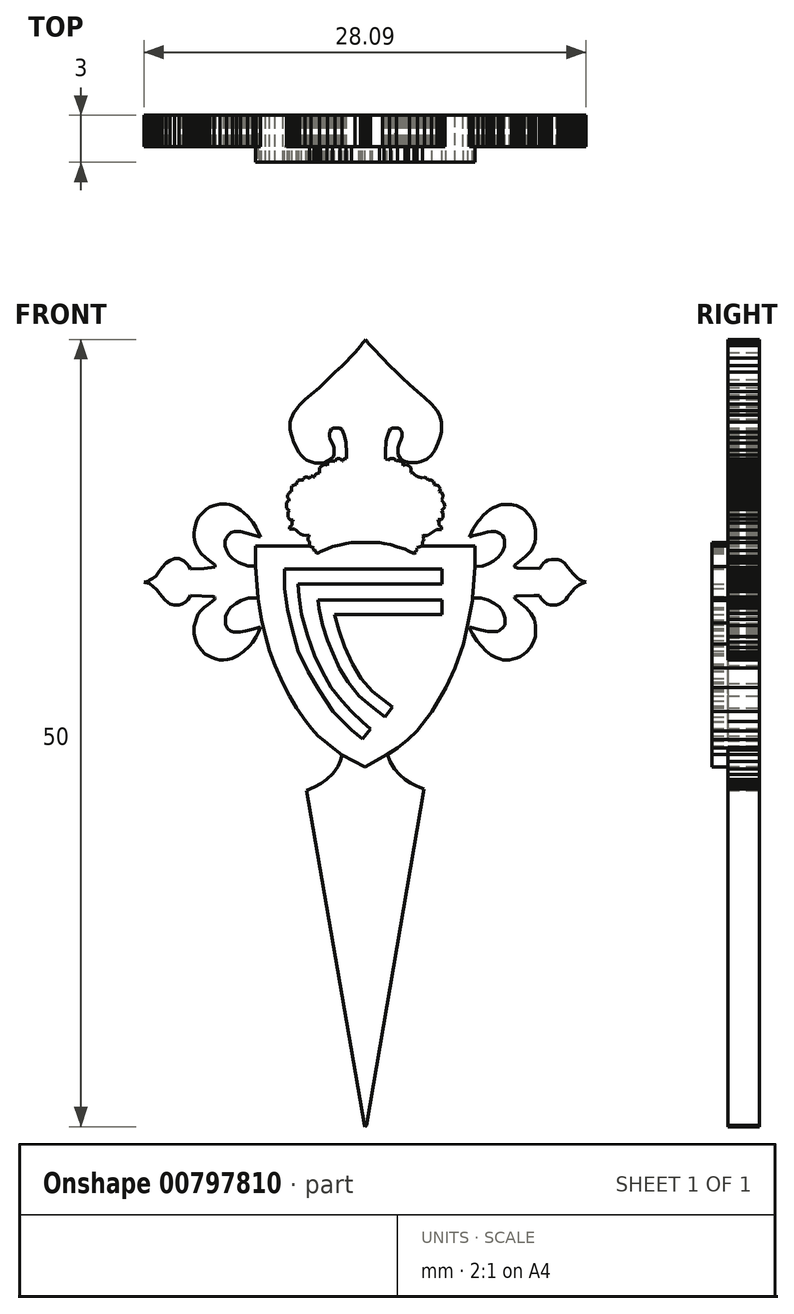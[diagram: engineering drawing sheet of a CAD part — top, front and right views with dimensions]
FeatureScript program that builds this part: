
annotation { "Feature Type Name" : "Feature", "Feature Type Description" : "" }
export const myFeature = defineFeature(function(context is Context, id is Id, definition is map)
    precondition{}
    {
        {
            var Q0;
            Q0=qCreatedBy(makeId("Front.planeOp"),FACE);
            var sketch = newSketch(context, id + "F0", { "sketchPlane" : qUnion([Q0])});
            skLineSegment(sketch, "E0", {"start": v(14.06, 0) * mm, "end": v(10.39, 21.27) * mm});
            skPoint(sketch, "E0.startSnap0", {"position": v(14.06, -0.08) * mm});
            skLineSegment(sketch, "E1", {"start": v(10.39, 21.27) * mm, "end": v(10.9, 21.5) * mm});
            skLineSegment(sketch, "E2", {"start": v(10.9, 21.5) * mm, "end": v(11.32, 21.71) * mm});
            skLineSegment(sketch, "E3", {"start": v(11.32, 21.71) * mm, "end": v(11.67, 21.99) * mm});
            skLineSegment(sketch, "E4", {"start": v(11.67, 21.99) * mm, "end": v(12.06, 22.35) * mm});
            skLineSegment(sketch, "E5", {"start": v(12.06, 22.35) * mm, "end": v(12.39, 22.8) * mm});
            skLineSegment(sketch, "E6", {"start": v(12.39, 22.8) * mm, "end": v(12.57, 23.17) * mm});
            skLineSegment(sketch, "E7", {"start": v(12.57, 23.17) * mm, "end": v(12.65, 23.55) * mm});
            skLineSegment(sketch, "E8", {"start": v(12.65, 23.55) * mm, "end": v(11.92, 24.1) * mm});
            skLineSegment(sketch, "E9", {"start": v(11.92, 24.1) * mm, "end": v(11.54, 24.4) * mm});
            skLineSegment(sketch, "E10", {"start": v(11.54, 24.4) * mm, "end": v(11.15, 24.74) * mm});
            skLineSegment(sketch, "E11", {"start": v(11.15, 24.74) * mm, "end": v(10.71, 25.21) * mm});
            skLineSegment(sketch, "E12", {"start": v(10.71, 25.21) * mm, "end": v(10.37, 25.64) * mm});
            skLineSegment(sketch, "E13", {"start": v(10.37, 25.64) * mm, "end": v(9.75, 26.5) * mm});
            skLineSegment(sketch, "E14", {"start": v(9.75, 26.5) * mm, "end": v(9.3, 27.27) * mm});
            skLineSegment(sketch, "E15", {"start": v(9.3, 27.27) * mm, "end": v(8.9, 28.06) * mm});
            skLineSegment(sketch, "E16", {"start": v(8.9, 28.06) * mm, "end": v(8.4, 29.21) * mm});
            skLineSegment(sketch, "E17", {"start": v(8.4, 29.21) * mm, "end": v(8.05, 30.15) * mm});
            skLineSegment(sketch, "E18", {"start": v(8.05, 30.15) * mm, "end": v(7.79, 31.09) * mm});
            skLineSegment(sketch, "E19", {"start": v(7.79, 31.09) * mm, "end": v(7.54, 32.09) * mm});
            skLineSegment(sketch, "E20", {"start": v(7.54, 32.09) * mm, "end": v(7.4, 32.9) * mm});
            skLineSegment(sketch, "E21", {"start": v(7.4, 32.9) * mm, "end": v(7.32, 33.46) * mm});
            skLineSegment(sketch, "E22", {"start": v(7.32, 33.46) * mm, "end": v(7.32, 33.5) * mm});
            skLineSegment(sketch, "E23", {"start": v(6.97, 33.5) * mm, "end": v(6.72, 33.5) * mm});
            skLineSegment(sketch, "E24", {"start": v(6.72, 33.5) * mm, "end": v(6.45, 33.4) * mm});
            skLineSegment(sketch, "E25", {"start": v(6.45, 33.4) * mm, "end": v(6.24, 33.33) * mm});
            skLineSegment(sketch, "E26", {"start": v(6.24, 33.33) * mm, "end": v(5.92, 33.16) * mm});
            skLineSegment(sketch, "E27", {"start": v(5.92, 33.16) * mm, "end": v(5.56, 32.88) * mm});
            skLineSegment(sketch, "E28", {"start": v(5.56, 32.88) * mm, "end": v(5.37, 32.61) * mm});
            skLineSegment(sketch, "E29", {"start": v(5.37, 32.61) * mm, "end": v(5.26, 32.32) * mm});
            skLineSegment(sketch, "E30", {"start": v(5.26, 32.32) * mm, "end": v(5.26, 31.8) * mm});
            skLineSegment(sketch, "E31", {"start": v(5.26, 31.8) * mm, "end": v(5.39, 31.56) * mm});
            skLineSegment(sketch, "E32", {"start": v(5.39, 31.56) * mm, "end": v(5.58, 31.4) * mm});
            skLineSegment(sketch, "E33", {"start": v(5.58, 31.4) * mm, "end": v(5.77, 31.33) * mm});
            skLineSegment(sketch, "E34", {"start": v(5.77, 31.33) * mm, "end": v(6.17, 31.33) * mm});
            skLineSegment(sketch, "E35", {"start": v(6.17, 31.33) * mm, "end": v(6.53, 31.4) * mm});
            skLineSegment(sketch, "E36", {"start": v(6.53, 31.4) * mm, "end": v(6.9, 31.49) * mm});
            skLineSegment(sketch, "E37", {"start": v(6.9, 31.49) * mm, "end": v(7.47, 31.64) * mm});
            skLineSegment(sketch, "E38", {"start": v(7.47, 31.64) * mm, "end": v(7.36, 31.33) * mm});
            skLineSegment(sketch, "E39", {"start": v(7.36, 31.33) * mm, "end": v(7.18, 31.03) * mm});
            skLineSegment(sketch, "E40", {"start": v(7.18, 31.03) * mm, "end": v(6.97, 30.68) * mm});
            skLineSegment(sketch, "E41", {"start": v(6.97, 30.68) * mm, "end": v(6.76, 30.46) * mm});
            skLineSegment(sketch, "E42", {"start": v(6.76, 30.46) * mm, "end": v(6.38, 30.1) * mm});
            skLineSegment(sketch, "E43", {"start": v(6.38, 30.1) * mm, "end": v(6.03, 29.84) * mm});
            skLineSegment(sketch, "E44", {"start": v(6.03, 29.84) * mm, "end": v(5.67, 29.65) * mm});
            skLineSegment(sketch, "E45", {"start": v(5.67, 29.65) * mm, "end": v(5.37, 29.6) * mm});
            skLineSegment(sketch, "E46", {"start": v(5.37, 29.6) * mm, "end": v(5.12, 29.56) * mm});
            skLineSegment(sketch, "E47", {"start": v(5.12, 29.56) * mm, "end": v(4.88, 29.56) * mm});
            skLineSegment(sketch, "E48", {"start": v(4.88, 29.56) * mm, "end": v(4.65, 29.63) * mm});
            skLineSegment(sketch, "E49", {"start": v(4.65, 29.63) * mm, "end": v(4.4, 29.72) * mm});
            skLineSegment(sketch, "E50", {"start": v(4.4, 29.72) * mm, "end": v(3.96, 29.96) * mm});
            skLineSegment(sketch, "E51", {"start": v(3.96, 29.96) * mm, "end": v(3.7, 30.22) * mm});
            skLineSegment(sketch, "E52", {"start": v(3.7, 30.22) * mm, "end": v(3.45, 30.57) * mm});
            skLineSegment(sketch, "E53", {"start": v(3.45, 30.57) * mm, "end": v(3.3, 30.96) * mm});
            skLineSegment(sketch, "E54", {"start": v(3.3, 30.96) * mm, "end": v(3.24, 31.25) * mm});
            skLineSegment(sketch, "E55", {"start": v(3.24, 31.25) * mm, "end": v(3.24, 31.7) * mm});
            skLineSegment(sketch, "E56", {"start": v(3.51, 32.48) * mm, "end": v(3.7, 32.7) * mm});
            skLineSegment(sketch, "E57", {"start": v(3.7, 32.7) * mm, "end": v(3.89, 32.89) * mm});
            skLineSegment(sketch, "E58", {"start": v(3.89, 32.89) * mm, "end": v(4.12, 33.07) * mm});
            skLineSegment(sketch, "E59", {"start": v(4.12, 33.07) * mm, "end": v(4.55, 33.4) * mm});
            skLineSegment(sketch, "E60", {"start": v(4.55, 33.4) * mm, "end": v(4.58, 33.5) * mm});
            skLineSegment(sketch, "E61", {"start": v(4.58, 33.5) * mm, "end": v(4.55, 33.57) * mm});
            skLineSegment(sketch, "E62", {"start": v(4.55, 33.57) * mm, "end": v(4.45, 33.6) * mm});
            skLineSegment(sketch, "E63", {"start": v(4.45, 33.6) * mm, "end": v(3.02, 33.66) * mm});
            skLineSegment(sketch, "E64", {"start": v(3.02, 33.66) * mm, "end": v(2.88, 33.4) * mm});
            skLineSegment(sketch, "E65", {"start": v(2.88, 33.4) * mm, "end": v(2.7, 33.25) * mm});
            skLineSegment(sketch, "E66", {"start": v(2.7, 33.25) * mm, "end": v(2.47, 33.13) * mm});
            skLineSegment(sketch, "E67", {"start": v(2.47, 33.13) * mm, "end": v(2.3, 33.07) * mm});
            skLineSegment(sketch, "E68", {"start": v(2.3, 33.07) * mm, "end": v(1.97, 33.07) * mm});
            skLineSegment(sketch, "E69", {"start": v(1.97, 33.07) * mm, "end": v(1.73, 33.12) * mm});
            skLineSegment(sketch, "E70", {"start": v(1.73, 33.12) * mm, "end": v(1.59, 33.23) * mm});
            skLineSegment(sketch, "E71", {"start": v(1.59, 33.23) * mm, "end": v(1.39, 33.4) * mm});
            skLineSegment(sketch, "E72", {"start": v(1.39, 33.4) * mm, "end": v(1.1, 33.76) * mm});
            skLineSegment(sketch, "E73", {"start": v(1.1, 33.76) * mm, "end": v(0.87, 34.05) * mm});
            skLineSegment(sketch, "E74", {"start": v(0.87, 34.05) * mm, "end": v(0.66, 34.23) * mm});
            skLineSegment(sketch, "E75", {"start": v(0.66, 34.23) * mm, "end": v(0.41, 34.4) * mm});
            skLineSegment(sketch, "E76", {"start": v(0.41, 34.4) * mm, "end": v(0.14, 34.49) * mm});
            skLineSegment(sketch, "E77", {"start": v(0.14, 34.49) * mm, "end": v(0.06, 34.5) * mm});
            skLineSegment(sketch, "E78", {"start": v(0.06, 34.5) * mm, "end": v(0.14, 34.52) * mm});
            skLineSegment(sketch, "E79", {"start": v(0.14, 34.52) * mm, "end": v(0.25, 34.55) * mm});
            skLineSegment(sketch, "E80", {"start": v(0.25, 34.55) * mm, "end": v(0.35, 34.59) * mm});
            skLineSegment(sketch, "E81", {"start": v(0.35, 34.59) * mm, "end": v(0.43, 34.64) * mm});
            skLineSegment(sketch, "E82", {"start": v(0.43, 34.64) * mm, "end": v(0.62, 34.74) * mm});
            skLineSegment(sketch, "E83", {"start": v(0.62, 34.74) * mm, "end": v(0.82, 34.91) * mm});
            skLineSegment(sketch, "E84", {"start": v(0.82, 34.91) * mm, "end": v(1.02, 35.17) * mm});
            skLineSegment(sketch, "E85", {"start": v(1.02, 35.17) * mm, "end": v(1.22, 35.44) * mm});
            skLineSegment(sketch, "E86", {"start": v(1.22, 35.44) * mm, "end": v(1.46, 35.7) * mm});
            skLineSegment(sketch, "E87", {"start": v(1.46, 35.7) * mm, "end": v(1.72, 35.9) * mm});
            skLineSegment(sketch, "E88", {"start": v(1.72, 35.9) * mm, "end": v(2, 36) * mm});
            skLineSegment(sketch, "E89", {"start": v(2, 36) * mm, "end": v(2.3, 36) * mm});
            skLineSegment(sketch, "E90", {"start": v(2.3, 36) * mm, "end": v(2.6, 35.84) * mm});
            skLineSegment(sketch, "E91", {"start": v(2.6, 35.84) * mm, "end": v(2.8, 35.67) * mm});
            skLineSegment(sketch, "E92", {"start": v(2.8, 35.67) * mm, "end": v(2.93, 35.5) * mm});
            skLineSegment(sketch, "E93", {"start": v(2.93, 35.5) * mm, "end": v(3.02, 35.35) * mm});
            skLineSegment(sketch, "E94", {"start": v(3.02, 35.35) * mm, "end": v(3.89, 35.39) * mm});
            skLineSegment(sketch, "E95", {"start": v(3.89, 35.39) * mm, "end": v(4.58, 35.46) * mm});
            skLineSegment(sketch, "E96", {"start": v(4.58, 35.46) * mm, "end": v(4.58, 35.56) * mm});
            skLineSegment(sketch, "E97", {"start": v(4.58, 35.56) * mm, "end": v(4.55, 35.62) * mm});
            skLineSegment(sketch, "E98", {"start": v(4.55, 35.62) * mm, "end": v(4.3, 35.8) * mm});
            skLineSegment(sketch, "E99", {"start": v(4.3, 35.8) * mm, "end": v(3.97, 36.09) * mm});
            skLineSegment(sketch, "E100", {"start": v(3.97, 36.09) * mm, "end": v(3.7, 36.33) * mm});
            skLineSegment(sketch, "E101", {"start": v(3.7, 36.33) * mm, "end": v(3.5, 36.6) * mm});
            skLineSegment(sketch, "E102", {"start": v(3.5, 36.6) * mm, "end": v(3.35, 36.91) * mm});
            skLineSegment(sketch, "E103", {"start": v(3.35, 36.91) * mm, "end": v(3.28, 37.17) * mm});
            skLineSegment(sketch, "E104", {"start": v(3.28, 37.17) * mm, "end": v(3.23, 37.4) * mm});
            skLineSegment(sketch, "E105", {"start": v(3.23, 37.4) * mm, "end": v(3.23, 37.58) * mm});
            skLineSegment(sketch, "E106", {"start": v(3.23, 37.58) * mm, "end": v(3.28, 37.88) * mm});
            skLineSegment(sketch, "E107", {"start": v(3.28, 37.88) * mm, "end": v(3.34, 38.12) * mm});
            skLineSegment(sketch, "E108", {"start": v(3.34, 38.12) * mm, "end": v(3.42, 38.4) * mm});
            skLineSegment(sketch, "E109", {"start": v(3.42, 38.4) * mm, "end": v(3.57, 38.67) * mm});
            skLineSegment(sketch, "E110", {"start": v(3.57, 38.67) * mm, "end": v(3.78, 38.9) * mm});
            skLineSegment(sketch, "E111", {"start": v(3.78, 38.9) * mm, "end": v(4.02, 39.12) * mm});
            skLineSegment(sketch, "E112", {"start": v(4.02, 39.12) * mm, "end": v(4.25, 39.27) * mm});
            skLineSegment(sketch, "E113", {"start": v(4.25, 39.27) * mm, "end": v(4.52, 39.38) * mm});
            skLineSegment(sketch, "E114", {"start": v(4.91, 39.48) * mm, "end": v(5.32, 39.48) * mm});
            skLineSegment(sketch, "E115", {"start": v(5.32, 39.48) * mm, "end": v(5.5, 39.43) * mm});
            skLineSegment(sketch, "E116", {"start": v(5.5, 39.43) * mm, "end": v(5.7, 39.36) * mm});
            skLineSegment(sketch, "E117", {"start": v(5.7, 39.36) * mm, "end": v(5.94, 39.25) * mm});
            skLineSegment(sketch, "E118", {"start": v(5.94, 39.25) * mm, "end": v(6.2, 39.1) * mm});
            skLineSegment(sketch, "E119", {"start": v(6.66, 38.7) * mm, "end": v(7, 38.3) * mm});
            skLineSegment(sketch, "E120", {"start": v(7, 38.3) * mm, "end": v(7.19, 37.98) * mm});
            skLineSegment(sketch, "E121", {"start": v(7.19, 37.98) * mm, "end": v(7.48, 37.38) * mm});
            skLineSegment(sketch, "E122", {"start": v(7.48, 37.38) * mm, "end": v(6.43, 37.67) * mm});
            skLineSegment(sketch, "E123", {"start": v(6.43, 37.67) * mm, "end": v(6.22, 37.73) * mm});
            skLineSegment(sketch, "E124", {"start": v(6.22, 37.73) * mm, "end": v(5.83, 37.73) * mm});
            skLineSegment(sketch, "E125", {"start": v(5.83, 37.73) * mm, "end": v(5.6, 37.67) * mm});
            skLineSegment(sketch, "E126", {"start": v(5.6, 37.67) * mm, "end": v(5.4, 37.48) * mm});
            skLineSegment(sketch, "E127", {"start": v(5.4, 37.48) * mm, "end": v(5.27, 37.27) * mm});
            skLineSegment(sketch, "E128", {"start": v(5.27, 37.27) * mm, "end": v(5.23, 37.12) * mm});
            skLineSegment(sketch, "E129", {"start": v(5.23, 37.12) * mm, "end": v(5.23, 36.8) * mm});
            skLineSegment(sketch, "E130", {"start": v(5.23, 36.8) * mm, "end": v(5.31, 36.55) * mm});
            skLineSegment(sketch, "E131", {"start": v(5.31, 36.55) * mm, "end": v(5.48, 36.23) * mm});
            skLineSegment(sketch, "E132", {"start": v(5.48, 36.23) * mm, "end": v(5.7, 36) * mm});
            skLineSegment(sketch, "E133", {"start": v(5.7, 36) * mm, "end": v(6.08, 35.75) * mm});
            skLineSegment(sketch, "E134", {"start": v(6.08, 35.75) * mm, "end": v(6.67, 35.52) * mm});
            skLineSegment(sketch, "E135", {"start": v(6.67, 35.52) * mm, "end": v(7.16, 35.52) * mm});
            skLineSegment(sketch, "E136", {"start": v(7.16, 35.52) * mm, "end": v(7.16, 36.8) * mm});
            skLineSegment(sketch, "E137", {"start": v(10.58, 36.8) * mm, "end": v(10.58, 37.07) * mm});
            skLineSegment(sketch, "E138", {"start": v(10.58, 37.07) * mm, "end": v(10.48, 37.16) * mm});
            skLineSegment(sketch, "E139", {"start": v(10.48, 37.16) * mm, "end": v(10.48, 37.34) * mm});
            skLineSegment(sketch, "E140", {"start": v(10.48, 37.34) * mm, "end": v(10.54, 37.4) * mm});
            skLineSegment(sketch, "E141", {"start": v(10.54, 37.4) * mm, "end": v(10.54, 37.5) * mm});
            skLineSegment(sketch, "E142", {"start": v(10.54, 37.5) * mm, "end": v(10.35, 37.47) * mm});
            skLineSegment(sketch, "E143", {"start": v(10.35, 37.47) * mm, "end": v(10.17, 37.49) * mm});
            skLineSegment(sketch, "E144", {"start": v(10.17, 37.49) * mm, "end": v(10.01, 37.57) * mm});
            skLineSegment(sketch, "E145", {"start": v(10.01, 37.57) * mm, "end": v(9.86, 37.7) * mm});
            skLineSegment(sketch, "E146", {"start": v(9.86, 37.7) * mm, "end": v(9.72, 37.8) * mm});
            skLineSegment(sketch, "E147", {"start": v(9.72, 37.8) * mm, "end": v(9.64, 37.87) * mm});
            skLineSegment(sketch, "E148", {"start": v(9.64, 37.87) * mm, "end": v(9.3, 37.87) * mm});
            skLineSegment(sketch, "E149", {"start": v(9.3, 37.87) * mm, "end": v(9.3, 38) * mm});
            skLineSegment(sketch, "E150", {"start": v(9.3, 38) * mm, "end": v(9.48, 38.14) * mm});
            skLineSegment(sketch, "E151", {"start": v(9.48, 38.14) * mm, "end": v(9.48, 38.37) * mm});
            skLineSegment(sketch, "E152", {"start": v(9.48, 38.37) * mm, "end": v(9.54, 38.4) * mm});
            skLineSegment(sketch, "E153", {"start": v(9.54, 38.4) * mm, "end": v(9.54, 38.45) * mm});
            skLineSegment(sketch, "E154", {"start": v(9.54, 38.45) * mm, "end": v(9.43, 38.45) * mm});
            skLineSegment(sketch, "E155", {"start": v(9.43, 38.45) * mm, "end": v(9.34, 38.5) * mm});
            skLineSegment(sketch, "E156", {"start": v(9.34, 38.5) * mm, "end": v(9.3, 38.53) * mm});
            skLineSegment(sketch, "E157", {"start": v(9.3, 38.53) * mm, "end": v(9.2, 38.65) * mm});
            skLineSegment(sketch, "E158", {"start": v(9.2, 38.65) * mm, "end": v(9.2, 38.92) * mm});
            skLineSegment(sketch, "E159", {"start": v(9.2, 38.92) * mm, "end": v(9.24, 38.98) * mm});
            skLineSegment(sketch, "E160", {"start": v(9.24, 38.98) * mm, "end": v(9.3, 39.05) * mm});
            skLineSegment(sketch, "E161", {"start": v(9.3, 39.05) * mm, "end": v(9.22, 39.11) * mm});
            skLineSegment(sketch, "E162", {"start": v(9.22, 39.11) * mm, "end": v(9.13, 39.2) * mm});
            skLineSegment(sketch, "E163", {"start": v(9.13, 39.2) * mm, "end": v(9.1, 39.26) * mm});
            skLineSegment(sketch, "E164", {"start": v(9.1, 39.26) * mm, "end": v(9.1, 39.52) * mm});
            skLineSegment(sketch, "E165", {"start": v(9.1, 39.52) * mm, "end": v(9.13, 39.58) * mm});
            skLineSegment(sketch, "E166", {"start": v(9.13, 39.58) * mm, "end": v(9.18, 39.62) * mm});
            skLineSegment(sketch, "E167", {"start": v(9.18, 39.62) * mm, "end": v(9.23, 39.66) * mm});
            skLineSegment(sketch, "E168", {"start": v(9.23, 39.66) * mm, "end": v(9.3, 39.66) * mm});
            skLineSegment(sketch, "E169", {"start": v(9.3, 39.66) * mm, "end": v(9.3, 39.74) * mm});
            skLineSegment(sketch, "E170", {"start": v(9.3, 39.74) * mm, "end": v(9.25, 39.8) * mm});
            skLineSegment(sketch, "E171", {"start": v(9.25, 39.8) * mm, "end": v(9.2, 39.87) * mm});
            skLineSegment(sketch, "E172", {"start": v(9.2, 39.87) * mm, "end": v(9.2, 40.03) * mm});
            skLineSegment(sketch, "E173", {"start": v(9.2, 40.03) * mm, "end": v(9.24, 40.1) * mm});
            skLineSegment(sketch, "E174", {"start": v(9.24, 40.1) * mm, "end": v(9.27, 40.16) * mm});
            skLineSegment(sketch, "E175", {"start": v(9.27, 40.16) * mm, "end": v(9.33, 40.2) * mm});
            skLineSegment(sketch, "E176", {"start": v(9.33, 40.2) * mm, "end": v(9.38, 40.25) * mm});
            skLineSegment(sketch, "E177", {"start": v(9.38, 40.25) * mm, "end": v(9.43, 40.26) * mm});
            skLineSegment(sketch, "E178", {"start": v(9.43, 40.26) * mm, "end": v(9.43, 40.5) * mm});
            skLineSegment(sketch, "E179", {"start": v(9.43, 40.5) * mm, "end": v(9.48, 40.6) * mm});
            skLineSegment(sketch, "E180", {"start": v(9.48, 40.6) * mm, "end": v(9.59, 40.66) * mm});
            skLineSegment(sketch, "E181", {"start": v(9.59, 40.66) * mm, "end": v(9.64, 40.7) * mm});
            skLineSegment(sketch, "E182", {"start": v(9.64, 40.7) * mm, "end": v(9.77, 40.7) * mm});
            skLineSegment(sketch, "E183", {"start": v(9.77, 40.7) * mm, "end": v(9.77, 40.85) * mm});
            skLineSegment(sketch, "E184", {"start": v(9.77, 40.85) * mm, "end": v(9.8, 40.9) * mm});
            skLineSegment(sketch, "E185", {"start": v(9.8, 40.9) * mm, "end": v(9.86, 40.95) * mm});
            skLineSegment(sketch, "E186", {"start": v(9.86, 40.95) * mm, "end": v(9.9, 41) * mm});
            skLineSegment(sketch, "E187", {"start": v(9.9, 41) * mm, "end": v(10.14, 41) * mm});
            skLineSegment(sketch, "E188", {"start": v(10.14, 41) * mm, "end": v(10.21, 41.03) * mm});
            skLineSegment(sketch, "E189", {"start": v(10.21, 41.03) * mm, "end": v(10.21, 41.1) * mm});
            skLineSegment(sketch, "E190", {"start": v(10.21, 41.1) * mm, "end": v(10.27, 41.14) * mm});
            skLineSegment(sketch, "E191", {"start": v(10.27, 41.14) * mm, "end": v(10.34, 41.17) * mm});
            skLineSegment(sketch, "E192", {"start": v(10.34, 41.17) * mm, "end": v(10.42, 41.17) * mm});
            skLineSegment(sketch, "E193", {"start": v(10.42, 41.17) * mm, "end": v(10.47, 41.16) * mm});
            skLineSegment(sketch, "E194", {"start": v(10.47, 41.16) * mm, "end": v(10.54, 41.12) * mm});
            skLineSegment(sketch, "E195", {"start": v(10.54, 41.12) * mm, "end": v(10.58, 41.1) * mm});
            skLineSegment(sketch, "E196", {"start": v(10.58, 41.1) * mm, "end": v(10.6, 41.16) * mm});
            skLineSegment(sketch, "E197", {"start": v(10.6, 41.16) * mm, "end": v(10.65, 41.2) * mm});
            skLineSegment(sketch, "E198", {"start": v(10.65, 41.2) * mm, "end": v(10.7, 41.24) * mm});
            skLineSegment(sketch, "E199", {"start": v(10.7, 41.24) * mm, "end": v(10.74, 41.24) * mm});
            skLineSegment(sketch, "E200", {"start": v(10.74, 41.24) * mm, "end": v(10.8, 41.22) * mm});
            skLineSegment(sketch, "E201", {"start": v(10.8, 41.22) * mm, "end": v(10.84, 41.18) * mm});
            skLineSegment(sketch, "E202", {"start": v(10.84, 41.18) * mm, "end": v(10.89, 41.17) * mm});
            skLineSegment(sketch, "E203", {"start": v(10.89, 41.17) * mm, "end": v(10.89, 41.23) * mm});
            skLineSegment(sketch, "E204", {"start": v(10.89, 41.23) * mm, "end": v(10.92, 41.29) * mm});
            skLineSegment(sketch, "E205", {"start": v(10.92, 41.29) * mm, "end": v(10.94, 41.33) * mm});
            skLineSegment(sketch, "E206", {"start": v(10.94, 41.33) * mm, "end": v(11, 41.38) * mm});
            skLineSegment(sketch, "E207", {"start": v(11, 41.38) * mm, "end": v(11.05, 41.42) * mm});
            skLineSegment(sketch, "E208", {"start": v(11.05, 41.42) * mm, "end": v(11.1, 41.44) * mm});
            skLineSegment(sketch, "E209", {"start": v(11.1, 41.44) * mm, "end": v(11.23, 41.44) * mm});
            skLineSegment(sketch, "E210", {"start": v(11.23, 41.77) * mm, "end": v(11.28, 41.82) * mm});
            skLineSegment(sketch, "E211", {"start": v(11.28, 41.82) * mm, "end": v(11.33, 41.87) * mm});
            skLineSegment(sketch, "E212", {"start": v(11.33, 41.87) * mm, "end": v(11.4, 41.92) * mm});
            skLineSegment(sketch, "E213", {"start": v(11.4, 41.92) * mm, "end": v(11.47, 41.97) * mm});
            skLineSegment(sketch, "E214", {"start": v(11.47, 41.97) * mm, "end": v(11.66, 41.97) * mm});
            skLineSegment(sketch, "E215", {"start": v(11.66, 41.97) * mm, "end": v(11.73, 41.91) * mm});
            skLineSegment(sketch, "E216", {"start": v(11.73, 41.91) * mm, "end": v(11.73, 42.08) * mm});
            skLineSegment(sketch, "E217", {"start": v(11.73, 42.08) * mm, "end": v(11.86, 42.2) * mm});
            skLineSegment(sketch, "E218", {"start": v(11.86, 42.2) * mm, "end": v(12, 42.2) * mm});
            skLineSegment(sketch, "E219", {"start": v(12, 42.2) * mm, "end": v(12.13, 42.21) * mm});
            skLineSegment(sketch, "E220", {"start": v(12.13, 42.21) * mm, "end": v(12.2, 42.15) * mm});
            skLineSegment(sketch, "E221", {"start": v(12.2, 42.15) * mm, "end": v(12.23, 42.24) * mm});
            skLineSegment(sketch, "E222", {"start": v(12.23, 42.24) * mm, "end": v(12.28, 42.31) * mm});
            skLineSegment(sketch, "E223", {"start": v(12.28, 42.31) * mm, "end": v(12.34, 42.36) * mm});
            skLineSegment(sketch, "E224", {"start": v(12.34, 42.36) * mm, "end": v(12.5, 42.36) * mm});
            skLineSegment(sketch, "E225", {"start": v(12.5, 42.36) * mm, "end": v(12.6, 42.3) * mm});
            skLineSegment(sketch, "E226", {"start": v(12.6, 42.3) * mm, "end": v(12.66, 42.27) * mm});
            skLineSegment(sketch, "E227", {"start": v(12.66, 42.27) * mm, "end": v(12.67, 42.2) * mm});
            skLineSegment(sketch, "E228", {"start": v(12.67, 42.2) * mm, "end": v(12.7, 42.2) * mm});
            skLineSegment(sketch, "E229", {"start": v(12.7, 42.2) * mm, "end": v(12.7, 42.26) * mm});
            skLineSegment(sketch, "E230", {"start": v(12.7, 42.26) * mm, "end": v(12.77, 42.32) * mm});
            skLineSegment(sketch, "E231", {"start": v(12.77, 42.32) * mm, "end": v(12.85, 42.36) * mm});
            skLineSegment(sketch, "E232", {"start": v(12.85, 42.36) * mm, "end": v(12.94, 42.36) * mm});
            skLineSegment(sketch, "E233", {"start": v(12.94, 42.36) * mm, "end": v(12.94, 42.68) * mm});
            skLineSegment(sketch, "E234", {"start": v(12.94, 42.68) * mm, "end": v(12.88, 43.4) * mm});
            skLineSegment(sketch, "E235", {"start": v(12.88, 43.4) * mm, "end": v(12.76, 43.89) * mm});
            skLineSegment(sketch, "E236", {"start": v(12.76, 43.89) * mm, "end": v(12.64, 44.2) * mm});
            skLineSegment(sketch, "E237", {"start": v(12.64, 44.2) * mm, "end": v(12.48, 44.3) * mm});
            skLineSegment(sketch, "E238", {"start": v(12.48, 44.3) * mm, "end": v(12.11, 44.3) * mm});
            skLineSegment(sketch, "E239", {"start": v(12.11, 44.3) * mm, "end": v(11.98, 44.23) * mm});
            skLineSegment(sketch, "E240", {"start": v(11.98, 44.23) * mm, "end": v(11.89, 44.08) * mm});
            skLineSegment(sketch, "E241", {"start": v(11.89, 44.08) * mm, "end": v(11.85, 43.94) * mm});
            skLineSegment(sketch, "E242", {"start": v(11.85, 43.94) * mm, "end": v(11.85, 43.79) * mm});
            skLineSegment(sketch, "E243", {"start": v(11.85, 43.79) * mm, "end": v(11.9, 43.59) * mm});
            skLineSegment(sketch, "E244", {"start": v(12.1, 43.2) * mm, "end": v(12.14, 43.02) * mm});
            skLineSegment(sketch, "E245", {"start": v(12.14, 43.02) * mm, "end": v(12.14, 42.66) * mm});
            skLineSegment(sketch, "E246", {"start": v(12.14, 42.66) * mm, "end": v(12.1, 42.48) * mm});
            skLineSegment(sketch, "E247", {"start": v(12.1, 42.48) * mm, "end": v(11.93, 42.31) * mm});
            skLineSegment(sketch, "E248", {"start": v(11.93, 42.31) * mm, "end": v(11.73, 42.21) * mm});
            skLineSegment(sketch, "E249", {"start": v(11.73, 42.21) * mm, "end": v(11.61, 42.15) * mm});
            skLineSegment(sketch, "E250", {"start": v(11.61, 42.15) * mm, "end": v(11.46, 42.08) * mm});
            skLineSegment(sketch, "E251", {"start": v(11.46, 42.08) * mm, "end": v(10.94, 42.08) * mm});
            skLineSegment(sketch, "E252", {"start": v(10.94, 42.08) * mm, "end": v(10.74, 42.14) * mm});
            skLineSegment(sketch, "E253", {"start": v(10.74, 42.14) * mm, "end": v(10.54, 42.2) * mm});
            skLineSegment(sketch, "E254", {"start": v(10.54, 42.2) * mm, "end": v(10.4, 42.27) * mm});
            skLineSegment(sketch, "E255", {"start": v(10.4, 42.27) * mm, "end": v(10.22, 42.4) * mm});
            skLineSegment(sketch, "E256", {"start": v(10.22, 42.4) * mm, "end": v(10.09, 42.55) * mm});
            skLineSegment(sketch, "E257", {"start": v(10.09, 42.55) * mm, "end": v(9.91, 42.73) * mm});
            skLineSegment(sketch, "E258", {"start": v(9.57, 43.41) * mm, "end": v(9.5, 43.65) * mm});
            skLineSegment(sketch, "E259", {"start": v(9.5, 43.65) * mm, "end": v(9.43, 43.84) * mm});
            skLineSegment(sketch, "E260", {"start": v(9.43, 43.84) * mm, "end": v(9.34, 44.2) * mm});
            skLineSegment(sketch, "E261", {"start": v(9.34, 44.2) * mm, "end": v(9.34, 44.68) * mm});
            skLineSegment(sketch, "E262", {"start": v(9.34, 44.68) * mm, "end": v(9.38, 44.77) * mm});
            skLineSegment(sketch, "E263", {"start": v(9.38, 44.77) * mm, "end": v(9.4, 44.86) * mm});
            skLineSegment(sketch, "E264", {"start": v(9.4, 44.86) * mm, "end": v(9.5, 45.1) * mm});
            skLineSegment(sketch, "E265", {"start": v(9.5, 45.1) * mm, "end": v(9.6, 45.3) * mm});
            skLineSegment(sketch, "E266", {"start": v(9.6, 45.3) * mm, "end": v(9.7, 45.4) * mm});
            skLineSegment(sketch, "E267", {"start": v(9.7, 45.4) * mm, "end": v(9.85, 45.62) * mm});
            skLineSegment(sketch, "E268", {"start": v(9.85, 45.62) * mm, "end": v(9.96, 45.76) * mm});
            skLineSegment(sketch, "E269", {"start": v(9.96, 45.76) * mm, "end": v(10.3, 46.1) * mm});
            skLineSegment(sketch, "E270", {"start": v(10.3, 46.1) * mm, "end": v(10.7, 46.41) * mm});
            skLineSegment(sketch, "E271", {"start": v(10.7, 46.41) * mm, "end": v(11.23, 46.87) * mm});
            skLineSegment(sketch, "E272", {"start": v(11.23, 46.87) * mm, "end": v(11.73, 47.36) * mm});
            skLineSegment(sketch, "E273", {"start": v(11.73, 47.36) * mm, "end": v(12.2, 47.85) * mm});
            skLineSegment(sketch, "E274", {"start": v(12.2, 47.85) * mm, "end": v(12.63, 48.23) * mm});
            skLineSegment(sketch, "E275", {"start": v(12.63, 48.23) * mm, "end": v(13.47, 49.09) * mm});
            skLineSegment(sketch, "E276", {"start": v(13.47, 49.09) * mm, "end": v(13.8, 49.5) * mm});
            skLineSegment(sketch, "E277", {"start": v(13.8, 49.5) * mm, "end": v(13.96, 49.68) * mm});
            skLineSegment(sketch, "E278", {"start": v(13.96, 49.68) * mm, "end": v(14.08, 49.83) * mm});
            skLineSegment(sketch, "E279", {"start": v(14.08, 49.83) * mm, "end": v(14.15, 49.92) * mm});
            skLineSegment(sketch, "E280", {"start": v(14.15, 49.92) * mm, "end": v(14.22, 49.81) * mm});
            skLineSegment(sketch, "E281", {"start": v(14.22, 49.81) * mm, "end": v(14.3, 49.7) * mm});
            skLineSegment(sketch, "E282", {"start": v(14.3, 49.7) * mm, "end": v(14.45, 49.53) * mm});
            skLineSegment(sketch, "E283", {"start": v(14.45, 49.53) * mm, "end": v(14.6, 49.37) * mm});
            skLineSegment(sketch, "E284", {"start": v(14.6, 49.37) * mm, "end": v(15.2, 48.73) * mm});
            skLineSegment(sketch, "E285", {"start": v(15.2, 48.73) * mm, "end": v(15.66, 48.26) * mm});
            skLineSegment(sketch, "E286", {"start": v(15.66, 48.26) * mm, "end": v(16.1, 47.84) * mm});
            skLineSegment(sketch, "E287", {"start": v(16.1, 47.84) * mm, "end": v(16.45, 47.5) * mm});
            skLineSegment(sketch, "E288", {"start": v(16.45, 47.5) * mm, "end": v(16.93, 47.06) * mm});
            skLineSegment(sketch, "E289", {"start": v(16.93, 47.06) * mm, "end": v(17.45, 46.62) * mm});
            skLineSegment(sketch, "E290", {"start": v(17.45, 46.62) * mm, "end": v(17.9, 46.23) * mm});
            skLineSegment(sketch, "E291", {"start": v(17.9, 46.23) * mm, "end": v(18.32, 45.81) * mm});
            skLineSegment(sketch, "E292", {"start": v(18.32, 45.81) * mm, "end": v(18.67, 45.4) * mm});
            skLineSegment(sketch, "E293", {"start": v(18.67, 45.4) * mm, "end": v(18.82, 45.12) * mm});
            skLineSegment(sketch, "E294", {"start": v(18.82, 45.12) * mm, "end": v(18.96, 44.69) * mm});
            skLineSegment(sketch, "E295", {"start": v(18.96, 44.69) * mm, "end": v(18.96, 44.04) * mm});
            skLineSegment(sketch, "E296", {"start": v(18.96, 44.04) * mm, "end": v(18.88, 43.7) * mm});
            skLineSegment(sketch, "E297", {"start": v(18.88, 43.7) * mm, "end": v(18.74, 43.33) * mm});
            skLineSegment(sketch, "E298", {"start": v(18.74, 43.33) * mm, "end": v(18.55, 42.9) * mm});
            skLineSegment(sketch, "E299", {"start": v(18.55, 42.9) * mm, "end": v(18.33, 42.6) * mm});
            skLineSegment(sketch, "E300", {"start": v(18.33, 42.6) * mm, "end": v(18.03, 42.33) * mm});
            skLineSegment(sketch, "E301", {"start": v(18.03, 42.33) * mm, "end": v(17.66, 42.15) * mm});
            skLineSegment(sketch, "E302", {"start": v(17.66, 42.15) * mm, "end": v(17.4, 42.09) * mm});
            skLineSegment(sketch, "E303", {"start": v(17.4, 42.09) * mm, "end": v(16.9, 42.09) * mm});
            skLineSegment(sketch, "E304", {"start": v(16.9, 42.09) * mm, "end": v(16.6, 42.2) * mm});
            skLineSegment(sketch, "E305", {"start": v(16.6, 42.2) * mm, "end": v(16.35, 42.37) * mm});
            skLineSegment(sketch, "E306", {"start": v(16.35, 42.37) * mm, "end": v(16.2, 42.63) * mm});
            skLineSegment(sketch, "E307", {"start": v(16.2, 42.63) * mm, "end": v(16.2, 43.07) * mm});
            skLineSegment(sketch, "E308", {"start": v(16.2, 43.07) * mm, "end": v(16.28, 43.35) * mm});
            skLineSegment(sketch, "E309", {"start": v(16.28, 43.35) * mm, "end": v(16.4, 43.55) * mm});
            skLineSegment(sketch, "E310", {"start": v(16.4, 43.55) * mm, "end": v(16.47, 43.75) * mm});
            skLineSegment(sketch, "E311", {"start": v(16.47, 43.75) * mm, "end": v(16.47, 44.01) * mm});
            skLineSegment(sketch, "E312", {"start": v(16.47, 44.01) * mm, "end": v(16.4, 44.14) * mm});
            skLineSegment(sketch, "E313", {"start": v(16.4, 44.14) * mm, "end": v(16.32, 44.24) * mm});
            skLineSegment(sketch, "E314", {"start": v(16.32, 44.24) * mm, "end": v(16.2, 44.3) * mm});
            skLineSegment(sketch, "E315", {"start": v(15.86, 44.3) * mm, "end": v(15.71, 44.24) * mm});
            skLineSegment(sketch, "E316", {"start": v(15.71, 44.24) * mm, "end": v(15.64, 44.08) * mm});
            skLineSegment(sketch, "E317", {"start": v(15.64, 44.08) * mm, "end": v(15.56, 43.9) * mm});
            skLineSegment(sketch, "E318", {"start": v(15.56, 43.9) * mm, "end": v(15.47, 43.59) * mm});
            skLineSegment(sketch, "E319", {"start": v(15.47, 43.59) * mm, "end": v(15.45, 43.43) * mm});
            skLineSegment(sketch, "E320", {"start": v(15.45, 43.43) * mm, "end": v(15.45, 43.23) * mm});
            skLineSegment(sketch, "E321", {"start": v(15.45, 43.23) * mm, "end": v(15.4, 43) * mm});
            skLineSegment(sketch, "E322", {"start": v(15.4, 42.32) * mm, "end": v(15.49, 42.32) * mm});
            skLineSegment(sketch, "E323", {"start": v(15.49, 42.32) * mm, "end": v(15.56, 42.28) * mm});
            skLineSegment(sketch, "E324", {"start": v(15.56, 42.28) * mm, "end": v(15.56, 42.23) * mm});
            skLineSegment(sketch, "E325", {"start": v(15.56, 42.23) * mm, "end": v(15.6, 42.27) * mm});
            skLineSegment(sketch, "E326", {"start": v(15.6, 42.27) * mm, "end": v(15.67, 42.32) * mm});
            skLineSegment(sketch, "E327", {"start": v(15.67, 42.32) * mm, "end": v(15.73, 42.36) * mm});
            skLineSegment(sketch, "E328", {"start": v(15.73, 42.36) * mm, "end": v(15.9, 42.36) * mm});
            skLineSegment(sketch, "E329", {"start": v(15.9, 42.36) * mm, "end": v(15.98, 42.31) * mm});
            skLineSegment(sketch, "E330", {"start": v(15.98, 42.31) * mm, "end": v(16.05, 42.26) * mm});
            skLineSegment(sketch, "E331", {"start": v(16.05, 42.26) * mm, "end": v(16.07, 42.2) * mm});
            skLineSegment(sketch, "E332", {"start": v(16.07, 42.2) * mm, "end": v(16.07, 42.18) * mm});
            skLineSegment(sketch, "E333", {"start": v(16.07, 42.18) * mm, "end": v(16.14, 42.22) * mm});
            skLineSegment(sketch, "E334", {"start": v(16.14, 42.22) * mm, "end": v(16.22, 42.23) * mm});
            skLineSegment(sketch, "E335", {"start": v(16.22, 42.23) * mm, "end": v(16.3, 42.2) * mm});
            skLineSegment(sketch, "E336", {"start": v(16.3, 42.2) * mm, "end": v(16.38, 42.2) * mm});
            skLineSegment(sketch, "E337", {"start": v(16.38, 42.2) * mm, "end": v(16.45, 42.16) * mm});
            skLineSegment(sketch, "E338", {"start": v(16.45, 42.16) * mm, "end": v(16.5, 42.09) * mm});
            skLineSegment(sketch, "E339", {"start": v(16.5, 42.09) * mm, "end": v(16.53, 42.04) * mm});
            skLineSegment(sketch, "E340", {"start": v(16.53, 42.04) * mm, "end": v(16.53, 41.91) * mm});
            skLineSegment(sketch, "E341", {"start": v(16.53, 41.91) * mm, "end": v(16.6, 41.94) * mm});
            skLineSegment(sketch, "E342", {"start": v(16.6, 41.94) * mm, "end": v(16.72, 41.98) * mm});
            skLineSegment(sketch, "E343", {"start": v(16.72, 41.98) * mm, "end": v(16.8, 41.95) * mm});
            skLineSegment(sketch, "E344", {"start": v(16.8, 41.95) * mm, "end": v(16.9, 41.9) * mm});
            skLineSegment(sketch, "E345", {"start": v(16.9, 41.9) * mm, "end": v(17, 41.81) * mm});
            skLineSegment(sketch, "E346", {"start": v(17, 41.81) * mm, "end": v(17.03, 41.7) * mm});
            skLineSegment(sketch, "E347", {"start": v(17.03, 41.7) * mm, "end": v(17.03, 41.45) * mm});
            skLineSegment(sketch, "E348", {"start": v(17.03, 41.45) * mm, "end": v(17.15, 41.43) * mm});
            skLineSegment(sketch, "E349", {"start": v(17.15, 41.43) * mm, "end": v(17.22, 41.38) * mm});
            skLineSegment(sketch, "E350", {"start": v(17.22, 41.38) * mm, "end": v(17.4, 41.2) * mm});
            skLineSegment(sketch, "E351", {"start": v(17.4, 41.2) * mm, "end": v(17.43, 41.22) * mm});
            skLineSegment(sketch, "E352", {"start": v(17.76, 41.12) * mm, "end": v(17.84, 41.17) * mm});
            skLineSegment(sketch, "E353", {"start": v(17.84, 41.17) * mm, "end": v(17.9, 41.15) * mm});
            skLineSegment(sketch, "E354", {"start": v(17.9, 41.15) * mm, "end": v(17.98, 41.13) * mm});
            skLineSegment(sketch, "E355", {"start": v(17.98, 41.13) * mm, "end": v(18.03, 41.1) * mm});
            skLineSegment(sketch, "E356", {"start": v(18.03, 41.1) * mm, "end": v(18.07, 41.07) * mm});
            skLineSegment(sketch, "E357", {"start": v(18.07, 41.07) * mm, "end": v(18.1, 41) * mm});
            skLineSegment(sketch, "E358", {"start": v(18.1, 41) * mm, "end": v(18.1, 40.96) * mm});
            skLineSegment(sketch, "E359", {"start": v(18.1, 40.96) * mm, "end": v(18.15, 41) * mm});
            skLineSegment(sketch, "E360", {"start": v(18.15, 41) * mm, "end": v(18.3, 41) * mm});
            skLineSegment(sketch, "E361", {"start": v(18.3, 41) * mm, "end": v(18.36, 40.97) * mm});
            skLineSegment(sketch, "E362", {"start": v(18.36, 40.97) * mm, "end": v(18.4, 40.93) * mm});
            skLineSegment(sketch, "E363", {"start": v(18.4, 40.93) * mm, "end": v(18.44, 40.89) * mm});
            skLineSegment(sketch, "E364", {"start": v(18.44, 40.89) * mm, "end": v(18.48, 40.83) * mm});
            skLineSegment(sketch, "E365", {"start": v(18.48, 40.83) * mm, "end": v(18.5, 40.7) * mm});
            skLineSegment(sketch, "E366", {"start": v(18.5, 40.7) * mm, "end": v(18.74, 40.63) * mm});
            skLineSegment(sketch, "E367", {"start": v(18.74, 40.63) * mm, "end": v(18.9, 40.46) * mm});
            skLineSegment(sketch, "E368", {"start": v(18.9, 40.46) * mm, "end": v(18.8, 40.28) * mm});
            skLineSegment(sketch, "E369", {"start": v(18.8, 40.28) * mm, "end": v(18.96, 40.22) * mm});
            skLineSegment(sketch, "E370", {"start": v(18.96, 40.22) * mm, "end": v(19.08, 40) * mm});
            skLineSegment(sketch, "E371", {"start": v(19.08, 40) * mm, "end": v(19.02, 39.83) * mm});
            skLineSegment(sketch, "E372", {"start": v(19.02, 39.83) * mm, "end": v(18.97, 39.7) * mm});
            skLineSegment(sketch, "E373", {"start": v(18.97, 39.7) * mm, "end": v(19.13, 39.53) * mm});
            skLineSegment(sketch, "E374", {"start": v(19.13, 39.53) * mm, "end": v(19.18, 39.32) * mm});
            skLineSegment(sketch, "E375", {"start": v(19.18, 39.32) * mm, "end": v(19.13, 39.2) * mm});
            skLineSegment(sketch, "E376", {"start": v(19.13, 39.2) * mm, "end": v(18.96, 39.06) * mm});
            skLineSegment(sketch, "E377", {"start": v(18.96, 39.06) * mm, "end": v(19.06, 38.88) * mm});
            skLineSegment(sketch, "E378", {"start": v(19.06, 38.88) * mm, "end": v(19.06, 38.61) * mm});
            skLineSegment(sketch, "E379", {"start": v(19.06, 38.61) * mm, "end": v(18.97, 38.5) * mm});
            skLineSegment(sketch, "E380", {"start": v(18.97, 38.5) * mm, "end": v(18.74, 38.5) * mm});
            skLineSegment(sketch, "E381", {"start": v(18.74, 38.5) * mm, "end": v(18.8, 38.3) * mm});
            skLineSegment(sketch, "E382", {"start": v(18.8, 38.3) * mm, "end": v(18.82, 38.14) * mm});
            skLineSegment(sketch, "E383", {"start": v(18.82, 38.14) * mm, "end": v(18.96, 38) * mm});
            skLineSegment(sketch, "E384", {"start": v(18.96, 38) * mm, "end": v(18.96, 37.86) * mm});
            skLineSegment(sketch, "E385", {"start": v(18.96, 37.86) * mm, "end": v(18.64, 37.86) * mm});
            skLineSegment(sketch, "E386", {"start": v(18.64, 37.86) * mm, "end": v(18.18, 37.52) * mm});
            skLineSegment(sketch, "E387", {"start": v(18.18, 37.52) * mm, "end": v(18.07, 37.48) * mm});
            skLineSegment(sketch, "E388", {"start": v(18.07, 37.48) * mm, "end": v(17.78, 37.48) * mm});
            skLineSegment(sketch, "E389", {"start": v(17.78, 37.48) * mm, "end": v(17.77, 37.43) * mm});
            skLineSegment(sketch, "E390", {"start": v(17.77, 37.43) * mm, "end": v(17.84, 37.35) * mm});
            skLineSegment(sketch, "E391", {"start": v(17.84, 37.35) * mm, "end": v(17.84, 37.28) * mm});
            skLineSegment(sketch, "E392", {"start": v(17.84, 37.28) * mm, "end": v(17.86, 37.24) * mm});
            skLineSegment(sketch, "E393", {"start": v(17.86, 37.24) * mm, "end": v(17.84, 37.16) * mm});
            skLineSegment(sketch, "E394", {"start": v(17.84, 37.16) * mm, "end": v(17.77, 37.1) * mm});
            skLineSegment(sketch, "E395", {"start": v(17.77, 37.1) * mm, "end": v(17.77, 36.79) * mm});
            skLineSegment(sketch, "E396", {"start": v(17.77, 36.79) * mm, "end": v(20.72, 36.79) * mm});
            skLineSegment(sketch, "E397", {"start": v(21.1, 36.79) * mm, "end": v(20.72, 36.79) * mm});
            skLineSegment(sketch, "E398", {"start": v(14.06, 0) * mm, "end": v(14.1, -0.08) * mm});
            skLineSegment(sketch, "E399", {"start": v(14.1, -0.08) * mm, "end": v(14.19, 0) * mm});
            skLineSegment(sketch, "E400", {"start": v(14.19, 0) * mm, "end": v(17.87, 21.36) * mm});
            skLineSegment(sketch, "E401", {"start": v(17.87, 21.36) * mm, "end": v(17.6, 21.46) * mm});
            skLineSegment(sketch, "E402", {"start": v(17.6, 21.46) * mm, "end": v(17.31, 21.6) * mm});
            skLineSegment(sketch, "E403", {"start": v(17.31, 21.6) * mm, "end": v(17, 21.74) * mm});
            skLineSegment(sketch, "E404", {"start": v(17, 21.74) * mm, "end": v(16.65, 21.99) * mm});
            skLineSegment(sketch, "E405", {"start": v(16.65, 21.99) * mm, "end": v(16.3, 22.3) * mm});
            skLineSegment(sketch, "E406", {"start": v(16.3, 22.3) * mm, "end": v(16, 22.64) * mm});
            skLineSegment(sketch, "E407", {"start": v(16, 22.64) * mm, "end": v(15.7, 23.1) * mm});
            skLineSegment(sketch, "E408", {"start": v(15.7, 23.1) * mm, "end": v(15.55, 23.56) * mm});
            skLineSegment(sketch, "E409", {"start": v(15.55, 23.56) * mm, "end": v(16.19, 24) * mm});
            skLineSegment(sketch, "E410", {"start": v(16.19, 24) * mm, "end": v(16.83, 24.5) * mm});
            skLineSegment(sketch, "E411", {"start": v(16.83, 24.5) * mm, "end": v(17.41, 25.06) * mm});
            skLineSegment(sketch, "E412", {"start": v(17.41, 25.06) * mm, "end": v(17.87, 25.65) * mm});
            skLineSegment(sketch, "E413", {"start": v(17.87, 25.65) * mm, "end": v(18.35, 26.29) * mm});
            skLineSegment(sketch, "E414", {"start": v(18.35, 26.29) * mm, "end": v(19.24, 27.82) * mm});
            skLineSegment(sketch, "E415", {"start": v(19.24, 27.82) * mm, "end": v(19.8, 29.06) * mm});
            skLineSegment(sketch, "E416", {"start": v(19.8, 29.06) * mm, "end": v(20.34, 30.6) * mm});
            skLineSegment(sketch, "E417", {"start": v(20.34, 30.6) * mm, "end": v(20.65, 31.92) * mm});
            skLineSegment(sketch, "E418", {"start": v(20.65, 31.92) * mm, "end": v(20.93, 33.35) * mm});
            skLineSegment(sketch, "E419", {"start": v(20.93, 33.35) * mm, "end": v(20.93, 33.5) * mm});
            skLineSegment(sketch, "E420", {"start": v(20.93, 33.5) * mm, "end": v(21.46, 33.5) * mm});
            skLineSegment(sketch, "E421", {"start": v(21.46, 33.5) * mm, "end": v(21.93, 33.37) * mm});
            skLineSegment(sketch, "E422", {"start": v(21.93, 33.37) * mm, "end": v(22.33, 33.17) * mm});
            skLineSegment(sketch, "E423", {"start": v(22.33, 33.17) * mm, "end": v(22.65, 32.93) * mm});
            skLineSegment(sketch, "E424", {"start": v(22.65, 32.93) * mm, "end": v(22.85, 32.6) * mm});
            skLineSegment(sketch, "E425", {"start": v(22.85, 32.6) * mm, "end": v(22.98, 32.23) * mm});
            skLineSegment(sketch, "E426", {"start": v(22.98, 32.23) * mm, "end": v(22.98, 31.78) * mm});
            skLineSegment(sketch, "E427", {"start": v(22.98, 31.78) * mm, "end": v(22.84, 31.59) * mm});
            skLineSegment(sketch, "E428", {"start": v(21.91, 31.36) * mm, "end": v(21.46, 31.46) * mm});
            skLineSegment(sketch, "E429", {"start": v(21.46, 31.46) * mm, "end": v(20.74, 31.65) * mm});
            skLineSegment(sketch, "E430", {"start": v(20.74, 31.65) * mm, "end": v(20.76, 31.57) * mm});
            skLineSegment(sketch, "E431", {"start": v(20.76, 31.57) * mm, "end": v(20.8, 31.47) * mm});
            skLineSegment(sketch, "E432", {"start": v(20.8, 31.47) * mm, "end": v(20.93, 31.22) * mm});
            skLineSegment(sketch, "E433", {"start": v(20.93, 31.22) * mm, "end": v(21.2, 30.78) * mm});
            skLineSegment(sketch, "E434", {"start": v(21.2, 30.78) * mm, "end": v(21.78, 30.12) * mm});
            skLineSegment(sketch, "E435", {"start": v(21.78, 30.12) * mm, "end": v(22.1, 29.88) * mm});
            skLineSegment(sketch, "E436", {"start": v(22.1, 29.88) * mm, "end": v(22.42, 29.71) * mm});
            skLineSegment(sketch, "E437", {"start": v(22.42, 29.71) * mm, "end": v(22.7, 29.61) * mm});
            skLineSegment(sketch, "E438", {"start": v(22.7, 29.61) * mm, "end": v(22.87, 29.56) * mm});
            skLineSegment(sketch, "E439", {"start": v(22.87, 29.56) * mm, "end": v(23.27, 29.56) * mm});
            skLineSegment(sketch, "E440", {"start": v(23.27, 29.56) * mm, "end": v(23.5, 29.61) * mm});
            skLineSegment(sketch, "E441", {"start": v(23.5, 29.61) * mm, "end": v(23.76, 29.68) * mm});
            skLineSegment(sketch, "E442", {"start": v(23.76, 29.68) * mm, "end": v(23.99, 29.8) * mm});
            skLineSegment(sketch, "E443", {"start": v(23.99, 29.8) * mm, "end": v(24.22, 29.95) * mm});
            skLineSegment(sketch, "E444", {"start": v(24.22, 29.95) * mm, "end": v(24.35, 30.06) * mm});
            skLineSegment(sketch, "E445", {"start": v(24.35, 30.06) * mm, "end": v(24.61, 30.35) * mm});
            skLineSegment(sketch, "E446", {"start": v(24.61, 30.35) * mm, "end": v(24.8, 30.7) * mm});
            skLineSegment(sketch, "E447", {"start": v(24.8, 30.7) * mm, "end": v(24.95, 31.07) * mm});
            skLineSegment(sketch, "E448", {"start": v(24.95, 31.07) * mm, "end": v(24.95, 31.76) * mm});
            skLineSegment(sketch, "E449", {"start": v(24.95, 31.76) * mm, "end": v(24.85, 32.14) * mm});
            skLineSegment(sketch, "E450", {"start": v(24.85, 32.14) * mm, "end": v(24.65, 32.52) * mm});
            skLineSegment(sketch, "E451", {"start": v(24.65, 32.52) * mm, "end": v(24.37, 32.86) * mm});
            skLineSegment(sketch, "E452", {"start": v(24.37, 32.86) * mm, "end": v(24.04, 33.13) * mm});
            skLineSegment(sketch, "E453", {"start": v(24.04, 33.13) * mm, "end": v(23.66, 33.43) * mm});
            skLineSegment(sketch, "E454", {"start": v(23.66, 33.43) * mm, "end": v(23.62, 33.48) * mm});
            skLineSegment(sketch, "E455", {"start": v(23.62, 33.48) * mm, "end": v(23.61, 33.56) * mm});
            skLineSegment(sketch, "E456", {"start": v(23.61, 33.56) * mm, "end": v(23.68, 33.61) * mm});
            skLineSegment(sketch, "E457", {"start": v(23.68, 33.61) * mm, "end": v(23.78, 33.62) * mm});
            skLineSegment(sketch, "E458", {"start": v(23.78, 33.62) * mm, "end": v(24.84, 33.67) * mm});
            skLineSegment(sketch, "E459", {"start": v(24.84, 33.67) * mm, "end": v(25.2, 33.67) * mm});
            skLineSegment(sketch, "E460", {"start": v(25.2, 33.67) * mm, "end": v(25.3, 33.46) * mm});
            skLineSegment(sketch, "E461", {"start": v(25.3, 33.46) * mm, "end": v(25.47, 33.26) * mm});
            skLineSegment(sketch, "E462", {"start": v(25.47, 33.26) * mm, "end": v(25.67, 33.13) * mm});
            skLineSegment(sketch, "E463", {"start": v(25.67, 33.13) * mm, "end": v(25.88, 33.06) * mm});
            skLineSegment(sketch, "E464", {"start": v(25.88, 33.06) * mm, "end": v(26.28, 33.06) * mm});
            skLineSegment(sketch, "E465", {"start": v(26.28, 33.06) * mm, "end": v(26.45, 33.11) * mm});
            skLineSegment(sketch, "E466", {"start": v(26.45, 33.11) * mm, "end": v(26.67, 33.23) * mm});
            skLineSegment(sketch, "E467", {"start": v(26.67, 33.23) * mm, "end": v(26.86, 33.4) * mm});
            skLineSegment(sketch, "E468", {"start": v(26.86, 33.4) * mm, "end": v(26.96, 33.56) * mm});
            skLineSegment(sketch, "E469", {"start": v(26.96, 33.56) * mm, "end": v(27.26, 33.92) * mm});
            skLineSegment(sketch, "E470", {"start": v(27.26, 33.92) * mm, "end": v(27.45, 34.13) * mm});
            skLineSegment(sketch, "E471", {"start": v(27.45, 34.13) * mm, "end": v(27.7, 34.32) * mm});
            skLineSegment(sketch, "E472", {"start": v(27.7, 34.32) * mm, "end": v(27.88, 34.43) * mm});
            skLineSegment(sketch, "E473", {"start": v(27.88, 34.43) * mm, "end": v(28.15, 34.51) * mm});
            skLineSegment(sketch, "E474", {"start": v(28.15, 34.51) * mm, "end": v(28.05, 34.54) * mm});
            skLineSegment(sketch, "E475", {"start": v(28.05, 34.54) * mm, "end": v(27.91, 34.58) * mm});
            skLineSegment(sketch, "E476", {"start": v(27.91, 34.58) * mm, "end": v(27.85, 34.62) * mm});
            skLineSegment(sketch, "E477", {"start": v(27.85, 34.62) * mm, "end": v(27.73, 34.67) * mm});
            skLineSegment(sketch, "E478", {"start": v(27.73, 34.67) * mm, "end": v(27.6, 34.77) * mm});
            skLineSegment(sketch, "E479", {"start": v(27.6, 34.77) * mm, "end": v(27.45, 34.92) * mm});
            skLineSegment(sketch, "E480", {"start": v(27.45, 34.92) * mm, "end": v(27.3, 35.05) * mm});
            skLineSegment(sketch, "E481", {"start": v(27.3, 35.05) * mm, "end": v(27.15, 35.24) * mm});
            skLineSegment(sketch, "E482", {"start": v(27.15, 35.24) * mm, "end": v(26.98, 35.45) * mm});
            skLineSegment(sketch, "E483", {"start": v(26.98, 35.45) * mm, "end": v(26.76, 35.72) * mm});
            skLineSegment(sketch, "E484", {"start": v(26.76, 35.72) * mm, "end": v(26.55, 35.87) * mm});
            skLineSegment(sketch, "E485", {"start": v(26.55, 35.87) * mm, "end": v(26.38, 35.96) * mm});
            skLineSegment(sketch, "E486", {"start": v(26.38, 35.96) * mm, "end": v(25.94, 35.96) * mm});
            skLineSegment(sketch, "E487", {"start": v(25.94, 35.96) * mm, "end": v(25.73, 35.9) * mm});
            skLineSegment(sketch, "E488", {"start": v(25.73, 35.9) * mm, "end": v(25.58, 35.82) * mm});
            skLineSegment(sketch, "E489", {"start": v(25.58, 35.82) * mm, "end": v(25.44, 35.73) * mm});
            skLineSegment(sketch, "E490", {"start": v(25.44, 35.73) * mm, "end": v(25.34, 35.6) * mm});
            skLineSegment(sketch, "E491", {"start": v(25.34, 35.6) * mm, "end": v(25.22, 35.4) * mm});
            skLineSegment(sketch, "E492", {"start": v(25.22, 35.4) * mm, "end": v(25.2, 35.37) * mm});
            skLineSegment(sketch, "E493", {"start": v(25.2, 35.37) * mm, "end": v(23.8, 35.42) * mm});
            skLineSegment(sketch, "E494", {"start": v(23.8, 35.42) * mm, "end": v(23.64, 35.46) * mm});
            skLineSegment(sketch, "E495", {"start": v(23.64, 35.46) * mm, "end": v(23.6, 35.5) * mm});
            skLineSegment(sketch, "E496", {"start": v(23.6, 35.5) * mm, "end": v(23.6, 35.57) * mm});
            skLineSegment(sketch, "E497", {"start": v(23.6, 35.57) * mm, "end": v(23.65, 35.62) * mm});
            skLineSegment(sketch, "E498", {"start": v(23.65, 35.62) * mm, "end": v(24.3, 36.12) * mm});
            skLineSegment(sketch, "E499", {"start": v(24.3, 36.12) * mm, "end": v(24.69, 36.52) * mm});
            skLineSegment(sketch, "E500", {"start": v(24.69, 36.52) * mm, "end": v(24.89, 37) * mm});
            skLineSegment(sketch, "E501", {"start": v(24.89, 37) * mm, "end": v(24.95, 37.32) * mm});
            skLineSegment(sketch, "E502", {"start": v(24.95, 37.32) * mm, "end": v(24.95, 37.8) * mm});
            skLineSegment(sketch, "E503", {"start": v(24.95, 37.8) * mm, "end": v(24.85, 38.26) * mm});
            skLineSegment(sketch, "E504", {"start": v(24.85, 38.26) * mm, "end": v(24.71, 38.52) * mm});
            skLineSegment(sketch, "E505", {"start": v(24.71, 38.52) * mm, "end": v(24.54, 38.76) * mm});
            skLineSegment(sketch, "E506", {"start": v(24.54, 38.76) * mm, "end": v(24.2, 39.1) * mm});
            skLineSegment(sketch, "E507", {"start": v(24.2, 39.1) * mm, "end": v(24.1, 39.17) * mm});
            skLineSegment(sketch, "E508", {"start": v(24.1, 39.17) * mm, "end": v(23.9, 39.28) * mm});
            skLineSegment(sketch, "E509", {"start": v(23.9, 39.28) * mm, "end": v(23.74, 39.37) * mm});
            skLineSegment(sketch, "E510", {"start": v(23.74, 39.37) * mm, "end": v(23.54, 39.41) * mm});
            skLineSegment(sketch, "E511", {"start": v(23.54, 39.41) * mm, "end": v(23.41, 39.45) * mm});
            skLineSegment(sketch, "E512", {"start": v(23.41, 39.45) * mm, "end": v(22.87, 39.45) * mm});
            skLineSegment(sketch, "E513", {"start": v(22.87, 39.45) * mm, "end": v(22.76, 39.42) * mm});
            skLineSegment(sketch, "E514", {"start": v(22.76, 39.42) * mm, "end": v(22.58, 39.37) * mm});
            skLineSegment(sketch, "E515", {"start": v(22.58, 39.37) * mm, "end": v(22.46, 39.32) * mm});
            skLineSegment(sketch, "E516", {"start": v(22.46, 39.32) * mm, "end": v(22.26, 39.24) * mm});
            skLineSegment(sketch, "E517", {"start": v(22.26, 39.24) * mm, "end": v(22.05, 39.12) * mm});
            skLineSegment(sketch, "E518", {"start": v(22.05, 39.12) * mm, "end": v(21.85, 38.96) * mm});
            skLineSegment(sketch, "E519", {"start": v(21.85, 38.96) * mm, "end": v(21.61, 38.73) * mm});
            skLineSegment(sketch, "E520", {"start": v(21.61, 38.73) * mm, "end": v(21.42, 38.5) * mm});
            skLineSegment(sketch, "E521", {"start": v(21.42, 38.5) * mm, "end": v(21.3, 38.34) * mm});
            skLineSegment(sketch, "E522", {"start": v(21.3, 38.34) * mm, "end": v(20.96, 37.9) * mm});
            skLineSegment(sketch, "E523", {"start": v(20.96, 37.9) * mm, "end": v(20.75, 37.38) * mm});
            skLineSegment(sketch, "E524", {"start": v(20.75, 37.38) * mm, "end": v(21.01, 37.46) * mm});
            skLineSegment(sketch, "E525", {"start": v(21.01, 37.46) * mm, "end": v(21.46, 37.57) * mm});
            skLineSegment(sketch, "E526", {"start": v(21.46, 37.57) * mm, "end": v(21.88, 37.68) * mm});
            skLineSegment(sketch, "E527", {"start": v(21.88, 37.68) * mm, "end": v(22.1, 37.7) * mm});
            skLineSegment(sketch, "E528", {"start": v(22.1, 37.7) * mm, "end": v(22.4, 37.7) * mm});
            skLineSegment(sketch, "E529", {"start": v(22.4, 37.7) * mm, "end": v(22.48, 37.68) * mm});
            skLineSegment(sketch, "E530", {"start": v(22.48, 37.68) * mm, "end": v(22.55, 37.65) * mm});
            skLineSegment(sketch, "E531", {"start": v(22.55, 37.65) * mm, "end": v(22.67, 37.6) * mm});
            skLineSegment(sketch, "E532", {"start": v(22.67, 37.6) * mm, "end": v(22.82, 37.48) * mm});
            skLineSegment(sketch, "E533", {"start": v(22.82, 37.48) * mm, "end": v(22.95, 37.3) * mm});
            skLineSegment(sketch, "E534", {"start": v(22.95, 37.3) * mm, "end": v(22.98, 37.19) * mm});
            skLineSegment(sketch, "E535", {"start": v(22.98, 37.19) * mm, "end": v(22.98, 36.76) * mm});
            skLineSegment(sketch, "E536", {"start": v(22.98, 36.76) * mm, "end": v(22.87, 36.53) * mm});
            skLineSegment(sketch, "E537", {"start": v(22.87, 36.53) * mm, "end": v(22.8, 36.38) * mm});
            skLineSegment(sketch, "E538", {"start": v(22.8, 36.38) * mm, "end": v(22.68, 36.23) * mm});
            skLineSegment(sketch, "E539", {"start": v(22.68, 36.23) * mm, "end": v(22.6, 36.1) * mm});
            skLineSegment(sketch, "E540", {"start": v(22.6, 36.1) * mm, "end": v(22.26, 35.84) * mm});
            skLineSegment(sketch, "E541", {"start": v(22.26, 35.84) * mm, "end": v(21.97, 35.7) * mm});
            skLineSegment(sketch, "E542", {"start": v(21.97, 35.7) * mm, "end": v(21.61, 35.54) * mm});
            skLineSegment(sketch, "E543", {"start": v(21.61, 35.54) * mm, "end": v(21.54, 35.52) * mm});
            skLineSegment(sketch, "E544", {"start": v(21.54, 35.52) * mm, "end": v(21.1, 35.5) * mm});
            skLineSegment(sketch, "E545", {"start": v(3.24, 31.7) * mm, "end": v(3.51, 32.48) * mm});
            skLineSegment(sketch, "E546", {"start": v(7.32, 33.5) * mm, "end": v(6.97, 33.5) * mm});
            skLineSegment(sketch, "E547", {"start": v(4.52, 39.38) * mm, "end": v(4.91, 39.48) * mm});
            skLineSegment(sketch, "E548", {"start": v(6.2, 39.1) * mm, "end": v(6.66, 38.7) * mm});
            skLineSegment(sketch, "E549", {"start": v(7.16, 36.8) * mm, "end": v(10.58, 36.8) * mm});
            skLineSegment(sketch, "E550", {"start": v(11.23, 41.44) * mm, "end": v(11.23, 41.77) * mm});
            skLineSegment(sketch, "E551", {"start": v(11.9, 43.59) * mm, "end": v(12.1, 43.2) * mm});
            skLineSegment(sketch, "E552", {"start": v(9.91, 42.73) * mm, "end": v(9.57, 43.41) * mm});
            skLineSegment(sketch, "E553", {"start": v(15.4, 43) * mm, "end": v(15.4, 42.32) * mm});
            skLineSegment(sketch, "E554", {"start": v(15.86, 44.3) * mm, "end": v(16.2, 44.3) * mm});
            skLineSegment(sketch, "E555", {"start": v(17.43, 41.22) * mm, "end": v(17.76, 41.12) * mm});
            skLineSegment(sketch, "E556", {"start": v(22.84, 31.59) * mm, "end": v(22.57, 31.37) * mm});
            skLineSegment(sketch, "E557", {"start": v(22.57, 31.37) * mm, "end": v(21.91, 31.36) * mm});
            skLineSegment(sketch, "E558", {"start": v(21.1, 36.79) * mm, "end": v(21.1, 35.5) * mm});
            skSolve(sketch);
        }
        {
            var Q0;
            Q0=qCreatedBy(makeId("Front.planeOp"),FACE);
            var sketch = newSketch(context, id + "F1", { "sketchPlane" : qUnion([Q0])});
            skLineSegment(sketch, "E559", {"start": v(14.11, 22.77) * mm, "end": v(12.66, 23.54) * mm});
            skLineSegment(sketch, "E560", {"start": v(12.66, 23.54) * mm, "end": v(11.92, 24.1) * mm});
            skLineSegment(sketch, "E561", {"start": v(11.92, 24.1) * mm, "end": v(11.54, 24.41) * mm});
            skLineSegment(sketch, "E562", {"start": v(11.54, 24.41) * mm, "end": v(11.14, 24.75) * mm});
            skLineSegment(sketch, "E563", {"start": v(11.14, 24.75) * mm, "end": v(10.72, 25.2) * mm});
            skLineSegment(sketch, "E564", {"start": v(10.72, 25.2) * mm, "end": v(10.37, 25.65) * mm});
            skLineSegment(sketch, "E565", {"start": v(10.37, 25.65) * mm, "end": v(9.75, 26.5) * mm});
            skLineSegment(sketch, "E566", {"start": v(9.75, 26.5) * mm, "end": v(9.3, 27.27) * mm});
            skLineSegment(sketch, "E567", {"start": v(9.3, 27.27) * mm, "end": v(8.89, 28.06) * mm});
            skLineSegment(sketch, "E568", {"start": v(8.89, 28.06) * mm, "end": v(8.39, 29.21) * mm});
            skLineSegment(sketch, "E569", {"start": v(8.39, 29.21) * mm, "end": v(8.04, 30.15) * mm});
            skLineSegment(sketch, "E570", {"start": v(8.04, 30.15) * mm, "end": v(7.79, 31.09) * mm});
            skLineSegment(sketch, "E571", {"start": v(7.79, 31.09) * mm, "end": v(7.53, 32.1) * mm});
            skLineSegment(sketch, "E572", {"start": v(7.53, 32.1) * mm, "end": v(7.4, 32.9) * mm});
            skLineSegment(sketch, "E573", {"start": v(7.4, 32.9) * mm, "end": v(7.32, 33.46) * mm});
            skLineSegment(sketch, "E574", {"start": v(7.32, 33.46) * mm, "end": v(7.32, 33.5) * mm});
            skLineSegment(sketch, "E575", {"start": v(7.32, 33.5) * mm, "end": v(7.16, 35.51) * mm});
            skLineSegment(sketch, "E576", {"start": v(7.16, 35.51) * mm, "end": v(7.16, 36.8) * mm});
            skLineSegment(sketch, "E577", {"start": v(7.16, 36.8) * mm, "end": v(10.6, 36.8) * mm});
            skLineSegment(sketch, "E578", {"start": v(10.6, 36.8) * mm, "end": v(10.87, 36.67) * mm});
            skLineSegment(sketch, "E579", {"start": v(10.87, 36.67) * mm, "end": v(10.85, 36.63) * mm});
            skLineSegment(sketch, "E580", {"start": v(10.85, 36.63) * mm, "end": v(10.85, 36.55) * mm});
            skLineSegment(sketch, "E581", {"start": v(10.85, 36.55) * mm, "end": v(10.88, 36.53) * mm});
            skLineSegment(sketch, "E582", {"start": v(10.88, 36.53) * mm, "end": v(10.93, 36.54) * mm});
            skLineSegment(sketch, "E583", {"start": v(10.93, 36.54) * mm, "end": v(10.95, 36.53) * mm});
            skLineSegment(sketch, "E584", {"start": v(10.95, 36.53) * mm, "end": v(10.95, 36.44) * mm});
            skLineSegment(sketch, "E585", {"start": v(10.95, 36.44) * mm, "end": v(10.95, 36.4) * mm});
            skLineSegment(sketch, "E586", {"start": v(10.95, 36.4) * mm, "end": v(11.03, 36.35) * mm});
            skLineSegment(sketch, "E587", {"start": v(11.03, 36.35) * mm, "end": v(11.11, 36.35) * mm});
            skLineSegment(sketch, "E588", {"start": v(11.11, 36.35) * mm, "end": v(11.19, 36.4) * mm});
            skLineSegment(sketch, "E589", {"start": v(11.19, 36.4) * mm, "end": v(11.27, 36.45) * mm});
            skLineSegment(sketch, "E590", {"start": v(11.27, 36.45) * mm, "end": v(11.68, 36.62) * mm});
            skLineSegment(sketch, "E591", {"start": v(11.68, 36.62) * mm, "end": v(12.06, 36.75) * mm});
            skLineSegment(sketch, "E592", {"start": v(12.06, 36.75) * mm, "end": v(12.5, 36.88) * mm});
            skLineSegment(sketch, "E593", {"start": v(12.5, 36.88) * mm, "end": v(12.9, 36.97) * mm});
            skLineSegment(sketch, "E594", {"start": v(12.9, 36.97) * mm, "end": v(13.25, 37.01) * mm});
            skLineSegment(sketch, "E595", {"start": v(15.04, 37.01) * mm, "end": v(15.3, 36.96) * mm});
            skLineSegment(sketch, "E596", {"start": v(15.3, 36.96) * mm, "end": v(15.73, 36.9) * mm});
            skLineSegment(sketch, "E597", {"start": v(15.73, 36.9) * mm, "end": v(16.16, 36.75) * mm});
            skLineSegment(sketch, "E598", {"start": v(16.16, 36.75) * mm, "end": v(16.64, 36.6) * mm});
            skLineSegment(sketch, "E599", {"start": v(16.64, 36.6) * mm, "end": v(16.85, 36.5) * mm});
            skLineSegment(sketch, "E600", {"start": v(16.85, 36.5) * mm, "end": v(17.22, 36.33) * mm});
            skLineSegment(sketch, "E601", {"start": v(17.22, 36.33) * mm, "end": v(17.34, 36.39) * mm});
            skLineSegment(sketch, "E602", {"start": v(17.34, 36.39) * mm, "end": v(17.32, 36.54) * mm});
            skLineSegment(sketch, "E603", {"start": v(17.32, 36.54) * mm, "end": v(17.36, 36.55) * mm});
            skLineSegment(sketch, "E604", {"start": v(17.36, 36.55) * mm, "end": v(17.44, 36.62) * mm});
            skLineSegment(sketch, "E605", {"start": v(17.44, 36.62) * mm, "end": v(17.42, 36.7) * mm});
            skLineSegment(sketch, "E606", {"start": v(17.42, 36.7) * mm, "end": v(17.77, 36.79) * mm});
            skLineSegment(sketch, "E607", {"start": v(17.77, 36.79) * mm, "end": v(21.1, 36.79) * mm});
            skLineSegment(sketch, "E608", {"start": v(21.1, 36.79) * mm, "end": v(21.1, 35.5) * mm});
            skLineSegment(sketch, "E609", {"start": v(21.1, 35.5) * mm, "end": v(20.93, 33.5) * mm});
            skLineSegment(sketch, "E610", {"start": v(20.93, 33.5) * mm, "end": v(20.93, 33.35) * mm});
            skLineSegment(sketch, "E611", {"start": v(20.93, 33.35) * mm, "end": v(20.65, 31.92) * mm});
            skLineSegment(sketch, "E612", {"start": v(20.65, 31.92) * mm, "end": v(20.35, 30.59) * mm});
            skLineSegment(sketch, "E613", {"start": v(20.35, 30.59) * mm, "end": v(19.8, 29.06) * mm});
            skLineSegment(sketch, "E614", {"start": v(19.8, 29.06) * mm, "end": v(19.23, 27.8) * mm});
            skLineSegment(sketch, "E615", {"start": v(19.23, 27.8) * mm, "end": v(18.36, 26.3) * mm});
            skLineSegment(sketch, "E616", {"start": v(17.42, 25.07) * mm, "end": v(16.85, 24.53) * mm});
            skLineSegment(sketch, "E617", {"start": v(16.85, 24.53) * mm, "end": v(16.18, 23.99) * mm});
            skLineSegment(sketch, "E618", {"start": v(16.18, 23.99) * mm, "end": v(15.52, 23.56) * mm});
            skLineSegment(sketch, "E619", {"start": v(15.52, 23.56) * mm, "end": v(14.11, 22.77) * mm});
            skLineSegment(sketch, "E620", {"start": v(17.42, 25.07) * mm, "end": v(18.36, 26.3) * mm});
            skLineSegment(sketch, "E621", {"start": v(13.25, 37.01) * mm, "end": v(15.04, 37.01) * mm});
            skLineSegment(sketch, "E622", {"start": v(11.12, 33.36) * mm, "end": v(18.98, 33.36) * mm});
            skLineSegment(sketch, "E623", {"start": v(18.98, 32.46) * mm, "end": v(12.18, 32.46) * mm});
            skLineSegment(sketch, "E624", {"start": v(12.18, 32.46) * mm, "end": v(12.47, 31.43) * mm});
            skLineSegment(sketch, "E625", {"start": v(12.47, 31.43) * mm, "end": v(12.8, 30.4) * mm});
            skLineSegment(sketch, "E626", {"start": v(12.8, 30.4) * mm, "end": v(13.3, 29.31) * mm});
            skLineSegment(sketch, "E627", {"start": v(13.3, 29.31) * mm, "end": v(13.86, 28.39) * mm});
            skLineSegment(sketch, "E628", {"start": v(13.86, 28.39) * mm, "end": v(14.6, 27.58) * mm});
            skLineSegment(sketch, "E629", {"start": v(14.6, 27.58) * mm, "end": v(15.86, 26.57) * mm});
            skLineSegment(sketch, "E630", {"start": v(15.86, 26.57) * mm, "end": v(15.37, 25.94) * mm});
            skLineSegment(sketch, "E631", {"start": v(15.37, 25.94) * mm, "end": v(14.48, 26.64) * mm});
            skLineSegment(sketch, "E632", {"start": v(14.48, 26.64) * mm, "end": v(13.74, 27.3) * mm});
            skLineSegment(sketch, "E633", {"start": v(13.74, 27.3) * mm, "end": v(13.01, 28.18) * mm});
            skLineSegment(sketch, "E634", {"start": v(13.01, 28.18) * mm, "end": v(12.5, 29.03) * mm});
            skLineSegment(sketch, "E635", {"start": v(12.5, 29.03) * mm, "end": v(12.08, 29.97) * mm});
            skLineSegment(sketch, "E636", {"start": v(12.08, 29.97) * mm, "end": v(11.72, 30.82) * mm});
            skLineSegment(sketch, "E637", {"start": v(11.72, 30.82) * mm, "end": v(11.4, 31.79) * mm});
            skLineSegment(sketch, "E638", {"start": v(11.4, 31.79) * mm, "end": v(11.17, 32.83) * mm});
            skLineSegment(sketch, "E639", {"start": v(11.17, 32.83) * mm, "end": v(11.12, 33.36) * mm});
            skLineSegment(sketch, "E640", {"start": v(18.98, 33.36) * mm, "end": v(18.98, 32.46) * mm});
            skLineSegment(sketch, "E641", {"start": v(18.98, 35.35) * mm, "end": v(9, 35.35) * mm});
            skLineSegment(sketch, "E642", {"start": v(9, 35.35) * mm, "end": v(9, 34.1) * mm});
            skLineSegment(sketch, "E643", {"start": v(9, 34.1) * mm, "end": v(9.19, 32.78) * mm});
            skLineSegment(sketch, "E644", {"start": v(9.19, 32.78) * mm, "end": v(9.46, 31.56) * mm});
            skLineSegment(sketch, "E645", {"start": v(9.46, 31.56) * mm, "end": v(9.86, 30.15) * mm});
            skLineSegment(sketch, "E646", {"start": v(9.86, 30.15) * mm, "end": v(10.5, 28.84) * mm});
            skLineSegment(sketch, "E647", {"start": v(10.5, 28.84) * mm, "end": v(11.19, 27.64) * mm});
            skLineSegment(sketch, "E648", {"start": v(11.19, 27.64) * mm, "end": v(12.08, 26.3) * mm});
            skLineSegment(sketch, "E649", {"start": v(12.08, 26.3) * mm, "end": v(12.71, 25.65) * mm});
            skLineSegment(sketch, "E650", {"start": v(12.71, 25.65) * mm, "end": v(13.25, 25.12) * mm});
            skLineSegment(sketch, "E651", {"start": v(13.25, 25.12) * mm, "end": v(13.93, 24.55) * mm});
            skLineSegment(sketch, "E652", {"start": v(13.93, 24.55) * mm, "end": v(14.46, 25.19) * mm});
            skLineSegment(sketch, "E653", {"start": v(14.46, 25.19) * mm, "end": v(13.93, 25.63) * mm});
            skLineSegment(sketch, "E654", {"start": v(13.93, 25.63) * mm, "end": v(13.25, 26.3) * mm});
            skLineSegment(sketch, "E655", {"start": v(13.25, 26.3) * mm, "end": v(12.64, 26.96) * mm});
            skLineSegment(sketch, "E656", {"start": v(12.64, 26.96) * mm, "end": v(11.94, 27.83) * mm});
            skLineSegment(sketch, "E657", {"start": v(11.94, 27.83) * mm, "end": v(11.37, 28.87) * mm});
            skLineSegment(sketch, "E658", {"start": v(11.37, 28.87) * mm, "end": v(10.91, 29.85) * mm});
            skLineSegment(sketch, "E659", {"start": v(10.91, 29.85) * mm, "end": v(10.46, 31.1) * mm});
            skLineSegment(sketch, "E660", {"start": v(10.46, 31.1) * mm, "end": v(10.09, 32.46) * mm});
            skLineSegment(sketch, "E661", {"start": v(10.09, 32.46) * mm, "end": v(9.9, 33.6) * mm});
            skLineSegment(sketch, "E662", {"start": v(9.9, 33.6) * mm, "end": v(9.84, 34.37) * mm});
            skLineSegment(sketch, "E663", {"start": v(9.84, 34.37) * mm, "end": v(18.99, 34.37) * mm});
            skLineSegment(sketch, "E664", {"start": v(18.98, 35.35) * mm, "end": v(18.99, 34.37) * mm});
            skSolve(sketch);
        }
        {
            var Q0;
            Q0=qSketchRegion(id+"F0",true);
            extrude(context, id + "F2", {"entities" : qUnion([Q0]), "depth" : 2 * mm, "offsetDistance" : 25 * mm});
        }
        {
            var Q0;
            Q0=qSketchRegion(id+"F1",true);
            extrude(context, id + "F3", {"entities" : qUnion([Q0]), "operationType" : NewBodyOperationType.ADD, "depth" : 3 * mm, "offsetDistance" : 25 * mm});
        }
    });
